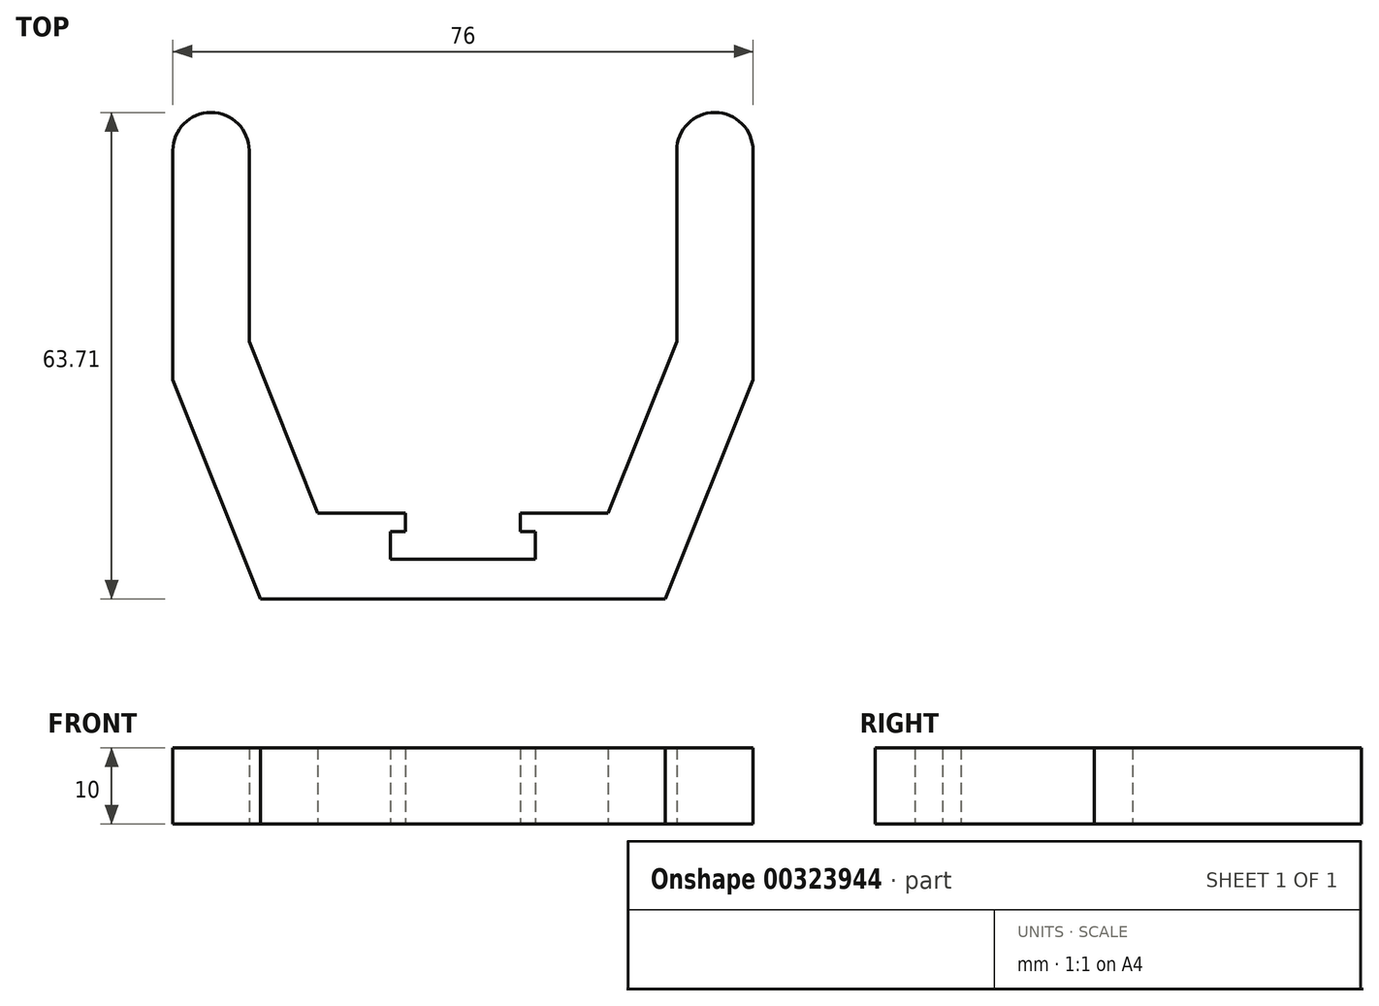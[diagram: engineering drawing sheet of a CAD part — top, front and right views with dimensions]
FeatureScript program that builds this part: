
annotation { "Feature Type Name" : "Feature", "Feature Type Description" : "" }
export const myFeature = defineFeature(function(context is Context, id is Id, definition is map)
    precondition{}
    {
        {
            var Q0;
            Q0=qCreatedBy(makeId("Top.planeOp"),FACE);
            var sketch = newSketch(context, id + "F0", { "sketchPlane" : qUnion([Q0])});
            skLineSegment(sketch, "E0", {"start": v(0, 0) * mm, "end": v(-9.5, 0) * mm});
            skLineSegment(sketch, "E1", {"start": v(-9.5, 0) * mm, "end": v(-9.5, 6) * mm});
            skLineSegment(sketch, "E2", {"start": v(-9.5, 6) * mm, "end": v(-7.5, 6) * mm});
            skLineSegment(sketch, "E3", {"start": v(-7.5, 6) * mm, "end": v(-7.5, 3.6) * mm});
            skLineSegment(sketch, "E4", {"start": v(-7.5, 3.6) * mm, "end": v(-9.5, 3.6) * mm});
            skLineSegment(sketch, "E5", {"start": v(-9.5, 6) * mm, "end": v(-11.5, 6) * mm});
            skLineSegment(sketch, "E6", {"start": v(-11.5, 6) * mm, "end": v(-11.5, 0) * mm});
            skLineSegment(sketch, "E7", {"start": v(-11.5, 0) * mm, "end": v(-9.5, 0) * mm});
            skLineSegment(sketch, "E8", {"start": v(-11.5, 0) * mm, "end": v(-11.5, -1.5) * mm});
            skLineSegment(sketch, "E9", {"start": v(-11.5, -1.5) * mm, "end": v(0, -1.5) * mm});
            skLineSegment(sketch, "E10", {"start": v(0, -1.5) * mm, "end": v(0, 0) * mm});
            skLineSegment(sketch, "E11.MirrorCS", {"start": v(0, 0) * mm, "end": v(9.5, 0) * mm});
            skLineSegment(sketch, "E12.MirrorCS", {"start": v(9.5, 0) * mm, "end": v(9.5, 6) * mm});
            skLineSegment(sketch, "E13.MirrorCS", {"start": v(9.5, 6) * mm, "end": v(7.5, 6) * mm});
            skLineSegment(sketch, "E14.MirrorCS", {"start": v(7.5, 6) * mm, "end": v(7.5, 3.6) * mm});
            skLineSegment(sketch, "E15.MirrorCS", {"start": v(11.5, -1.5) * mm, "end": v(0, -1.5) * mm});
            skLineSegment(sketch, "E16.MirrorCS", {"start": v(11.5, 6) * mm, "end": v(11.5, 0) * mm});
            skLineSegment(sketch, "E17.MirrorCS", {"start": v(7.5, 3.6) * mm, "end": v(9.5, 3.6) * mm});
            skLineSegment(sketch, "E18.MirrorCS", {"start": v(11.5, 0) * mm, "end": v(11.5, -1.5) * mm});
            skLineSegment(sketch, "E19.MirrorCS", {"start": v(11.5, 0) * mm, "end": v(9.5, 0) * mm});
            skLineSegment(sketch, "E20.MirrorCS", {"start": v(9.5, 6) * mm, "end": v(11.5, 6) * mm});
            skLineSegment(sketch, "E21", {"start": v(0, -1.5) * mm, "end": v(-38, -1.5) * mm});
            skLineSegment(sketch, "E22", {"start": v(0, -1.5) * mm, "end": v(38, -1.5) * mm});
            skLineSegment(sketch, "E23", {"start": v(-11.5, 6) * mm, "end": v(-38, 6) * mm});
            skLineSegment(sketch, "E24", {"start": v(11.5, 6) * mm, "end": v(38, 6) * mm});
            skLineSegment(sketch, "E25", {"start": v(38, 6) * mm, "end": v(38, -1.5) * mm});
            skLineSegment(sketch, "E26", {"start": v(-38, 6) * mm, "end": v(-38, -1.5) * mm});
            skPoint(sketch, "E27", {"position": v(-28, 6) * mm});
            skPoint(sketch, "E28", {"position": v(28, 6) * mm});
            skLineSegment(sketch, "E29", {"start": v(-28, 6) * mm, "end": v(-28, 53.5) * mm});
            skLineSegment(sketch, "E30", {"start": v(-38, 6) * mm, "end": v(-38, 53.5) * mm});
            skLineSegment(sketch, "E31", {"start": v(28, 6) * mm, "end": v(28, 53.5) * mm});
            skLineSegment(sketch, "E32", {"start": v(38, 6) * mm, "end": v(38, 53.5) * mm});
            skLineSegment(sketch, "E33", {"start": v(-38, 53.5) * mm, "end": v(-28, 53.5) * mm, "construction": true});
            skPoint(sketch, "E34", {"position": v(-33, 53.5) * mm});
            skArc(sketch, "E35", {"start": v(-38, 53.5) * mm, "mid": v(-33, 58.5) * mm, "end": v(-28, 53.5) * mm});
            skArc(sketch, "E36", {"start": v(28, 53.5) * mm, "mid": v(33, 58.5) * mm, "end": v(38, 53.5) * mm});
            skLineSegment(sketch, "E37", {"start": v(28, 53.5) * mm, "end": v(38, 53.5) * mm, "construction": true});
            skPoint(sketch, "E38", {"position": v(-28, -1.5) * mm});
            skPoint(sketch, "E39", {"position": v(-38, 23.5) * mm});
            skPoint(sketch, "E40", {"position": v(-16, -1.5) * mm});
            skLineSegment(sketch, "E41", {"start": v(-28, -1.5) * mm, "end": v(-38, 23.5) * mm});
            skLineSegment(sketch, "E42", {"start": v(-16, -1.5) * mm, "end": v(-28, 28.5) * mm});
            skLineSegment(sketch, "E43.MirrorCS", {"start": v(16, -1.5) * mm, "end": v(28, 28.5) * mm});
            skLineSegment(sketch, "E44.MirrorCS", {"start": v(28, -1.5) * mm, "end": v(38, 23.5) * mm});
            skLineSegment(sketch, "E45", {"start": v(-28, -1.5) * mm, "end": v(-26.51, -5.21) * mm});
            skLineSegment(sketch, "E46.MirrorCS", {"start": v(28, -1.5) * mm, "end": v(26.51, -5.21) * mm});
            skLineSegment(sketch, "E47", {"start": v(-26.51, -5.21) * mm, "end": v(26.51, -5.21) * mm});
            skSolve(sketch);
        }
        {
            var Q0;
            {var subQ0=sQuery(id+"F0.wireOp",EDGE,"E2");Q0=makeQuery(id+"F0.imprint","IMPRINT",FACE,{"disambiguationData":[TD([[makeQuery(id+"F0.imprint","IMPRINT",EDGE,{"derivedFrom":subQ0}),-1.0]])]});}
            var Q1;
            {var subQ0=sQuery(id+"F0.wireOp",EDGE,"E5");Q1=makeQuery(id+"F0.imprint","IMPRINT",FACE,{"disambiguationData":[TD([[makeQuery(id+"F0.imprint","IMPRINT",EDGE,{"derivedFrom":subQ0}),1.0]])]});}
            var Q2;
            Q2=makeQuery(id+"F0.imprint","IMPRINT",FACE,{"disambiguationData":[TD([[makeQuery(id+"F0.imprint","IMPRINT",EDGE,{"derivedFrom":sQuery(id+"F0.wireOp",EDGE,"E10")}),-1.0]])]});
            var Q3;
            {var subQ0=sQuery(id+"F0.wireOp",EDGE,"E13.MirrorCS");Q3=makeQuery(id+"F0.imprint","IMPRINT",FACE,{"disambiguationData":[TD([[makeQuery(id+"F0.imprint","IMPRINT",EDGE,{"derivedFrom":subQ0}),1.0]])]});}
            var Q4;
            Q4=makeQuery(id+"F0.imprint","IMPRINT",FACE,{"disambiguationData":[TD([[makeQuery(id+"F0.imprint","IMPRINT",EDGE,{"derivedFrom":sQuery(id+"F0.wireOp",EDGE,"E0")}),1.0]])]});
            var Q5;
            Q5=makeQuery(id+"F0.imprint","IMPRINT",FACE,{"disambiguationData":[TD([[makeQuery(id+"F0.imprint","IMPRINT",EDGE,{"derivedFrom":sQuery(id+"F0.wireOp",EDGE,"E16.MirrorCS")}),-1.0]])]});
            extrude(context, id + "F1", {"entities" : qUnion([Q0, Q1, Q2, Q3, Q4, Q5]), "depth" : 10 * mm});
        }
        {
            var Q0;
            {var subQ1=sQuery(id+"F0.wireOp",EDGE,"E6");Q0=makeQuery(id+"F0.imprint","IMPRINT",FACE,{"disambiguationData":[TD([[makeQuery(id+"F0.imprint","IMPRINT",EDGE,{"derivedFrom":subQ1}),-1.0]])]});}
            var Q1;
            {var subQ2=sQuery(id+"F0.wireOp",EDGE,"E29");Q1=makeQuery(id+"F0.imprint","IMPRINT",FACE,{"disambiguationData":[TD([[makeQuery(id+"F0.imprint","IMPRINT",EDGE,{"derivedFrom":subQ2}),1.0]])]});}
            var Q2;
            {var subQ1=sQuery(id+"F0.wireOp",EDGE,"E16.MirrorCS");Q2=makeQuery(id+"F0.imprint","IMPRINT",FACE,{"disambiguationData":[TD([[makeQuery(id+"F0.imprint","IMPRINT",EDGE,{"derivedFrom":subQ1}),1.0]])]});}
            var Q3;
            {var subQ2=sQuery(id+"F0.wireOp",EDGE,"E31");Q3=makeQuery(id+"F0.imprint","IMPRINT",FACE,{"disambiguationData":[TD([[makeQuery(id+"F0.imprint","IMPRINT",EDGE,{"derivedFrom":subQ2}),-1.0]])]});}
            var Q4;
            {var subQ0=sQuery(id+"F0.wireOp",EDGE,"E29");var subQ1=sQuery(id+"F0.wireOp",EDGE,"E23");var subQ2=makeQuery(id+"F0.imprint","INTERSECT",VERTEX,{"derivedFrom":[subQ1,subQ0]});Q4=makeQuery(id+"F0.imprint","IMPRINT",FACE,{"disambiguationData":[TD([[makeQuery(id+"F0.imprint","IMPRINT",EDGE,{"disambiguationData":[TD([[subQ2,1.0]])],"derivedFrom":subQ1}),-1.0]])]});}
            var Q5;
            {var subQ0=sQuery(id+"F0.wireOp",EDGE,"E41");var subQ1=sQuery(id+"F0.wireOp",EDGE,"E21");var subQ2=makeQuery(id+"F0.imprint","INTERSECT",VERTEX,{"derivedFrom":[subQ1,subQ0]});Q5=makeQuery(id+"F0.imprint","IMPRINT",FACE,{"disambiguationData":[TD([[makeQuery(id+"F0.imprint","IMPRINT",EDGE,{"disambiguationData":[TD([[subQ2,1.0]])],"derivedFrom":subQ1}),-1.0]])]});}
            var Q6;
            {var subQ0=sQuery(id+"F0.wireOp",EDGE,"E43.MirrorCS");var subQ1=sQuery(id+"F0.wireOp",EDGE,"E22");var subQ2=makeQuery(id+"F0.imprint","INTERSECT",VERTEX,{"derivedFrom":[subQ1,subQ0]});Q6=makeQuery(id+"F0.imprint","IMPRINT",FACE,{"disambiguationData":[TD([[makeQuery(id+"F0.imprint","IMPRINT",EDGE,{"disambiguationData":[TD([[subQ2,-1.0]])],"derivedFrom":subQ1}),1.0]])]});}
            var Q7;
            {var subQ0=sQuery(id+"F0.wireOp",EDGE,"E31");var subQ1=sQuery(id+"F0.wireOp",EDGE,"E24");var subQ2=makeQuery(id+"F0.imprint","INTERSECT",VERTEX,{"derivedFrom":[subQ1,subQ0]});Q7=makeQuery(id+"F0.imprint","IMPRINT",FACE,{"disambiguationData":[TD([[makeQuery(id+"F0.imprint","IMPRINT",EDGE,{"disambiguationData":[TD([[subQ2,1.0]])],"derivedFrom":subQ1}),1.0]])]});}
            var Q8;
            {var subQ5=sQuery(id+"F0.wireOp",EDGE,"E45");Q8=makeQuery(id+"F0.imprint","IMPRINT",FACE,{"disambiguationData":[TD([[makeQuery(id+"F0.imprint","IMPRINT",EDGE,{"derivedFrom":subQ5}),1.0]])]});}
            extrude(context, id + "F2", {"entities" : qUnion([Q0, Q1, Q2, Q3, Q4, Q5, Q6, Q7, Q8]), "operationType" : NewBodyOperationType.ADD, "depth" : 10 * mm});
        }
    });
